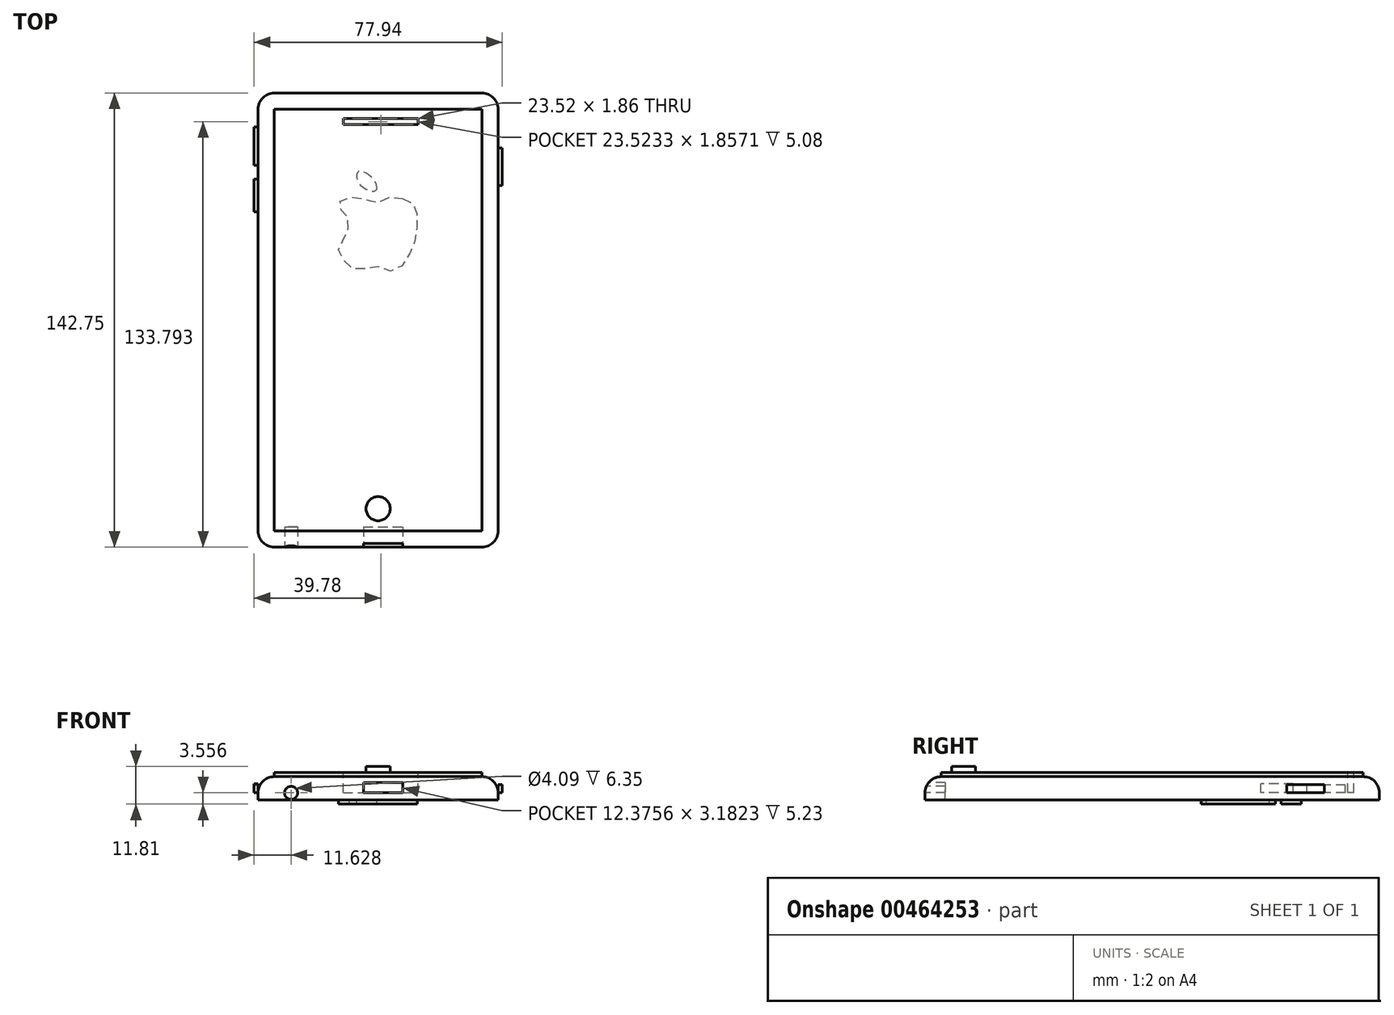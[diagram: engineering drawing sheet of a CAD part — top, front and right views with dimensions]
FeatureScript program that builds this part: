
annotation { "Feature Type Name" : "Feature", "Feature Type Description" : "" }
export const myFeature = defineFeature(function(context is Context, id is Id, definition is map)
    precondition{}
    {
        {
            var Q0;
            Q0=qCreatedBy(makeId("Top.planeOp"),FACE);
            var sketch = newSketch(context, id + "F0", { "sketchPlane" : qUnion([Q0])});
            skLineSegment(sketch, "E0.bottom", {"start": v(-63.9, 67.92) * mm, "end": v(11.51, 67.92) * mm});
            skLineSegment(sketch, "E0.top", {"start": v(-63.9, -74.83) * mm, "end": v(11.51, -74.83) * mm});
            skLineSegment(sketch, "E0.left", {"start": v(-63.9, 67.92) * mm, "end": v(-63.9, -74.83) * mm});
            skLineSegment(sketch, "E0.right", {"start": v(11.51, 67.92) * mm, "end": v(11.51, -74.83) * mm});
            skSolve(sketch);
        }
        {
            var Q0;
            Q0=makeQuery(id+"F0.imprint","IMPRINT",FACE,{"disambiguationData":[TD([[makeQuery(id+"F0.imprint","IMPRINT",EDGE,{"derivedFrom":sQuery(id+"F0.wireOp",EDGE,"E0.bottom")}),-1.0]])]});
            extrude(context, id + "F1", {"entities" : qUnion([Q0]), "depth" : 7.37 * mm});
        }
        {
            var Q0;
            Q0=makeQuery(id+"F1.opExtrude","CAP_FACE",FACE,{"disambiguationData":[OSD([sQuery(id+"F0.wireOp",EDGE,"E0.bottom"),sQuery(id+"F0.wireOp",EDGE,"E0.top"),sQuery(id+"F0.wireOp",EDGE,"E0.left"),sQuery(id+"F0.wireOp",EDGE,"E0.right")])],"isStart":false});
            var Q1;
            Q1=makeQuery(id+"F1.opExtrude","SWEPT_EDGE",EDGE,{"disambiguationData":[OSD([sQuery(id+"F0.wireOp",EDGE,"E0.top"),sQuery(id+"F0.wireOp",EDGE,"E0.left")])]});
            var Q2;
            Q2=makeQuery(id+"F1.opExtrude","SWEPT_EDGE",EDGE,{"disambiguationData":[OSD([sQuery(id+"F0.wireOp",EDGE,"E0.top"),sQuery(id+"F0.wireOp",EDGE,"E0.right")])]});
            var Q3;
            Q3=makeQuery(id+"F1.opExtrude","SWEPT_EDGE",EDGE,{"disambiguationData":[OSD([sQuery(id+"F0.wireOp",EDGE,"E0.bottom"),sQuery(id+"F0.wireOp",EDGE,"E0.left")])]});
            var Q4;
            Q4=makeQuery(id+"F1.opExtrude","SWEPT_EDGE",EDGE,{"disambiguationData":[OSD([sQuery(id+"F0.wireOp",EDGE,"E0.bottom"),sQuery(id+"F0.wireOp",EDGE,"E0.right")])]});
            fillet(context, id + "F2", {"entities" : qUnion([Q0, Q1, Q2, Q3, Q4]), "radius" : 5.08 * mm, "tangentPropagation" : true, "allowEdgeOverflow" : false});
        }
        {
            var Q0;
            Q0=makeQuery(id+"F1.opExtrude","SWEPT_FACE",FACE,{"disambiguationData":[OSD([sQuery(id+"F0.wireOp",EDGE,"E0.top")])]});
            var sketch = newSketch(context, id + "F3", { "sketchPlane" : qUnion([Q0])});
            skLineSegment(sketch, "E1.bottom", {"start": v(-30.8, 5.47) * mm, "end": v(-18.42, 5.47) * mm});
            skLineSegment(sketch, "E1.top", {"start": v(-30.8, 2.29) * mm, "end": v(-18.42, 2.29) * mm});
            skLineSegment(sketch, "E1.left", {"start": v(-30.8, 5.47) * mm, "end": v(-30.8, 2.29) * mm});
            skLineSegment(sketch, "E1.right", {"start": v(-18.42, 5.47) * mm, "end": v(-18.42, 2.29) * mm});
            skSolve(sketch);
        }
        {
            var Q0;
            Q0=makeQuery(id+"F3.imprint","IMPRINT",FACE,{"disambiguationData":[TD([[makeQuery(id+"F3.imprint","IMPRINT",EDGE,{"derivedFrom":sQuery(id+"F3.wireOp",EDGE,"E1.bottom")}),-1.0]])]});
            extrude(context, id + "F4", {"entities" : qUnion([Q0]), "operationType" : NewBodyOperationType.REMOVE, "oppositeDirection" : true, "depth" : 6.35 * mm});
        }
        {
            var Q0;
            Q0=makeQuery(id+"F1.opExtrude","SWEPT_FACE",FACE,{"disambiguationData":[OSD([sQuery(id+"F0.wireOp",EDGE,"E0.top")])]});
            var sketch = newSketch(context, id + "F5", { "sketchPlane" : qUnion([Q0])});
            skCircle(sketch, "E2", {"center": v(-53.53, 2.29) * mm, "radius": 2.05 * mm});
            skSolve(sketch);
        }
        {
            var Q0;
            Q0=qSketchRegion(id+"F5",true);
            extrude(context, id + "F6", {"entities" : qUnion([Q0]), "operationType" : NewBodyOperationType.REMOVE, "oppositeDirection" : true, "depth" : 6.35 * mm});
        }
        {
            var Q0;
            Q0=makeQuery(id+"F1.opExtrude","CAP_FACE",FACE,{"disambiguationData":[OSD([sQuery(id+"F0.wireOp",EDGE,"E0.bottom"),sQuery(id+"F0.wireOp",EDGE,"E0.top"),sQuery(id+"F0.wireOp",EDGE,"E0.left"),sQuery(id+"F0.wireOp",EDGE,"E0.right")])],"isStart":false});
            var sketch = newSketch(context, id + "F7", { "sketchPlane" : qUnion([Q0])});
            skLineSegment(sketch, "E3.bottom", {"start": v(-58.81, 62.84) * mm, "end": v(6.43, 62.84) * mm});
            skLineSegment(sketch, "E3.top", {"start": v(-58.81, -69.75) * mm, "end": v(6.43, -69.75) * mm});
            skLineSegment(sketch, "E3.left", {"start": v(-58.81, 62.84) * mm, "end": v(-58.81, -69.75) * mm});
            skLineSegment(sketch, "E3.right", {"start": v(6.43, 62.84) * mm, "end": v(6.43, -69.75) * mm});
            skSolve(sketch);
        }
        {
            var Q0;
            Q0=makeQuery(id+"F7.imprint","IMPRINT",FACE,{"disambiguationData":[TD([[makeQuery(id+"F7.imprint","IMPRINT",EDGE,{"derivedFrom":sQuery(id+"F7.wireOp",EDGE,"E3.bottom")}),1.0]])]});
            extrude(context, id + "F8", {"entities" : qUnion([Q0]), "depth" : 1.27 * mm});
        }
        {
            var Q0;
            Q0=makeQuery(id+"F1.opExtrude","SWEPT_FACE",FACE,{"disambiguationData":[OSD([sQuery(id+"F0.wireOp",EDGE,"E0.right")])]});
            var sketch = newSketch(context, id + "F9", { "sketchPlane" : qUnion([Q0])});
            skLineSegment(sketch, "E4.bottom", {"start": v(38.85, 2.29) * mm, "end": v(50.65, 2.29) * mm});
            skLineSegment(sketch, "E4.top", {"start": v(38.85, 4.9) * mm, "end": v(50.65, 4.9) * mm});
            skLineSegment(sketch, "E4.left", {"start": v(38.85, 2.29) * mm, "end": v(38.85, 4.9) * mm});
            skLineSegment(sketch, "E4.right", {"start": v(50.65, 2.29) * mm, "end": v(50.65, 4.9) * mm});
            skSolve(sketch);
        }
        {
            var Q0;
            Q0=qSketchRegion(id+"F9",true);
            extrude(context, id + "F10", {"entities" : qUnion([Q0]), "depth" : 1.27 * mm});
        }
        {
            var Q0;
            Q0=makeQuery(id+"F8.opExtrude","CAP_FACE",FACE,{"disambiguationData":[OSD([sQuery(id+"F7.wireOp",EDGE,"E3.bottom"),sQuery(id+"F7.wireOp",EDGE,"E3.top"),sQuery(id+"F7.wireOp",EDGE,"E3.left"),sQuery(id+"F7.wireOp",EDGE,"E3.right")])],"isStart":false});
            var sketch = newSketch(context, id + "F11", { "sketchPlane" : qUnion([Q0])});
            skCircle(sketch, "E5", {"center": v(-26.2, -62.74) * mm, "radius": 3.79 * mm});
            skPoint(sketch, "E5.centerSnap0", {"position": v(-26.2, -69.75) * mm});
            skSolve(sketch);
        }
        {
            var Q0;
            Q0=qSketchRegion(id+"F11",true);
            extrude(context, id + "F12", {"entities" : qUnion([Q0]), "depth" : 1.9 * mm});
        }
        {
            var Q0;
            Q0=makeQuery(id+"F8.opExtrude","CAP_FACE",FACE,{"disambiguationData":[OSD([sQuery(id+"F7.wireOp",EDGE,"E3.bottom"),sQuery(id+"F7.wireOp",EDGE,"E3.top"),sQuery(id+"F7.wireOp",EDGE,"E3.left"),sQuery(id+"F7.wireOp",EDGE,"E3.right")])],"isStart":false});
            var sketch = newSketch(context, id + "F13", { "sketchPlane" : qUnion([Q0])});
            skLineSegment(sketch, "E6.bottom", {"start": v(-37.14, 59.9) * mm, "end": v(-13.62, 59.9) * mm});
            skLineSegment(sketch, "E6.top", {"start": v(-37.14, 58.03) * mm, "end": v(-13.62, 58.03) * mm});
            skLineSegment(sketch, "E6.left", {"start": v(-37.14, 59.9) * mm, "end": v(-37.14, 58.03) * mm});
            skLineSegment(sketch, "E6.right", {"start": v(-13.62, 59.9) * mm, "end": v(-13.62, 58.03) * mm});
            skSolve(sketch);
        }
        {
            var Q0;
            Q0=makeQuery(id+"F13.imprint","IMPRINT",FACE,{"disambiguationData":[TD([[makeQuery(id+"F13.imprint","IMPRINT",EDGE,{"derivedFrom":sQuery(id+"F13.wireOp",EDGE,"E6.bottom")}),-1.0]])]});
            extrude(context, id + "F14", {"entities" : qUnion([Q0]), "operationType" : NewBodyOperationType.REMOVE, "oppositeDirection" : true, "depth" : 6.35 * mm});
        }
        {
            var Q0;
            Q0=makeQuery(id+"F1.opExtrude","SWEPT_FACE",FACE,{"disambiguationData":[OSD([sQuery(id+"F0.wireOp",EDGE,"E0.left")])]});
            var sketch = newSketch(context, id + "F15", { "sketchPlane" : qUnion([Q0])});
            skLineSegment(sketch, "E7.bottom", {"start": v(-57.26, 2.29) * mm, "end": v(-45.19, 2.29) * mm});
            skLineSegment(sketch, "E7.top", {"start": v(-57.26, 4.8) * mm, "end": v(-45.19, 4.8) * mm});
            skLineSegment(sketch, "E7.left", {"start": v(-57.26, 2.29) * mm, "end": v(-57.26, 4.8) * mm});
            skLineSegment(sketch, "E7.right", {"start": v(-45.19, 2.29) * mm, "end": v(-45.19, 4.8) * mm});
            skSolve(sketch);
        }
        {
            var Q0;
            Q0=makeQuery(id+"F15.imprint","IMPRINT",FACE,{"disambiguationData":[TD([[makeQuery(id+"F15.imprint","IMPRINT",EDGE,{"derivedFrom":sQuery(id+"F15.wireOp",EDGE,"E7.bottom")}),-1.0]])]});
            extrude(context, id + "F16", {"entities" : qUnion([Q0]), "depth" : 1.27 * mm});
        }
        {
            var Q0;
            Q0=makeQuery(id+"F1.opExtrude","SWEPT_FACE",FACE,{"disambiguationData":[OSD([sQuery(id+"F0.wireOp",EDGE,"E0.left")])]});
            var sketch = newSketch(context, id + "F17", { "sketchPlane" : qUnion([Q0])});
            skLineSegment(sketch, "E8.bottom", {"start": v(-40.86, 2.29) * mm, "end": v(-30.64, 2.29) * mm});
            skLineSegment(sketch, "E8.top", {"start": v(-40.86, 5.1) * mm, "end": v(-30.64, 5.1) * mm});
            skLineSegment(sketch, "E8.left", {"start": v(-40.86, 2.29) * mm, "end": v(-40.86, 5.1) * mm});
            skLineSegment(sketch, "E8.right", {"start": v(-30.64, 2.29) * mm, "end": v(-30.64, 5.1) * mm});
            skSolve(sketch);
        }
        {
            var Q0;
            Q0=makeQuery(id+"F17.imprint","IMPRINT",FACE,{"disambiguationData":[TD([[makeQuery(id+"F17.imprint","IMPRINT",EDGE,{"derivedFrom":sQuery(id+"F17.wireOp",EDGE,"E8.bottom")}),-1.0]])]});
            extrude(context, id + "F18", {"entities" : qUnion([Q0]), "depth" : 1.27 * mm});
        }
        {
            var Q0;
            Q0=makeQuery(id+"F1.opExtrude","CAP_FACE",FACE,{"disambiguationData":[OSD([sQuery(id+"F0.wireOp",EDGE,"E0.bottom"),sQuery(id+"F0.wireOp",EDGE,"E0.top"),sQuery(id+"F0.wireOp",EDGE,"E0.left"),sQuery(id+"F0.wireOp",EDGE,"E0.right")])],"isStart":true});
            var sketch = newSketch(context, id + "F19", { "sketchPlane" : qUnion([Q0])});
            skFitSpline(sketch, "E9", {"points": [v(-26.93, -37.3) * mm, v(-27.86, -41.01) * mm, v(-32.5, -43.18) * mm, v(-31.88, -39.15) * mm, v(-26.93, -37.3) * mm]});
            skFitSpline(sketch, "E10", {"points": [v(-18.57, -34.82) * mm, v(-14.86, -32.65) * mm, v(-13.93, -28.01) * mm, v(-14.55, -21.82) * mm, v(-16.71, -16.56) * mm, v(-21.36, -11.92) * mm, v(-26.93, -13.46) * mm, v(-32.19, -12.23) * mm, v(-36.21, -14.4) * mm, v(-38.69, -18.73) * mm, v(-37.45, -21.2) * mm, v(-35.28, -27.08) * mm, v(-36.52, -29.87) * mm, v(-38.38, -32.03) * mm, v(-37.14, -34.82) * mm, v(-31.88, -34.82) * mm, v(-29.4, -34.51) * mm, v(-26.93, -33.27) * mm, v(-23.83, -34.82) * mm, v(-18.57, -34.82) * mm]});
            skSolve(sketch);
        }
        {
            var Q0;
            Q0=makeQuery(id+"F19.imprint","IMPRINT",FACE,{"disambiguationData":[TD([[makeQuery(id+"F19.imprint","IMPRINT",EDGE,{"derivedFrom":sQuery(id+"F19.wireOp",EDGE,"E9")}),-1.0]])]});
            var Q1;
            Q1=makeQuery(id+"F19.imprint","IMPRINT",FACE,{"disambiguationData":[TD([[makeQuery(id+"F19.imprint","IMPRINT",EDGE,{"derivedFrom":sQuery(id+"F19.wireOp",EDGE,"E10")}),1.0]])]});
            extrude(context, id + "F20", {"entities" : qUnion([Q0, Q1]), "depth" : 1.27 * mm});
        }
    });
